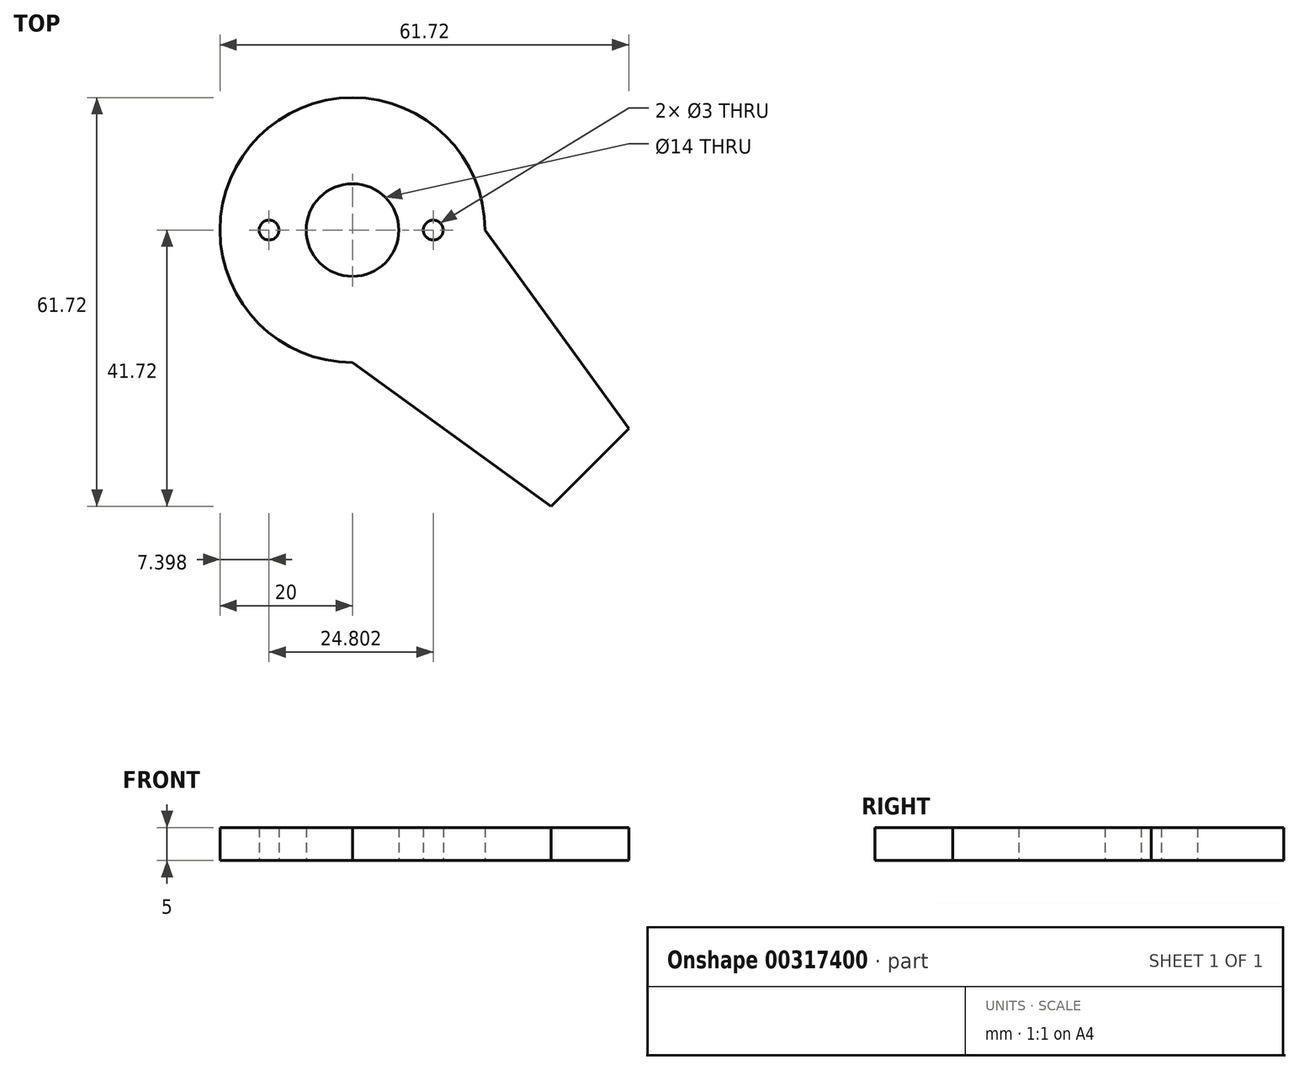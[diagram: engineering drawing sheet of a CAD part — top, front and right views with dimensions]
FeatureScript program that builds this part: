
annotation { "Feature Type Name" : "Feature", "Feature Type Description" : "" }
export const myFeature = defineFeature(function(context is Context, id is Id, definition is map)
    precondition{}
    {
        {
            var Q0;
            Q0=qCreatedBy(makeId("Top.planeOp"),FACE);
            var sketch = newSketch(context, id + "F0", { "sketchPlane" : qUnion([Q0])});
            skLineSegment(sketch, "E0.bottom", {"start": v(0, 0) * mm, "end": v(800, 0) * mm, "construction": true});
            skLineSegment(sketch, "E0.top", {"start": v(0, 800) * mm, "end": v(800, 800) * mm, "construction": true});
            skLineSegment(sketch, "E0.left", {"start": v(0, 0) * mm, "end": v(0, 800) * mm, "construction": true});
            skLineSegment(sketch, "E0.right", {"start": v(800, 0) * mm, "end": v(800, 800) * mm, "construction": true});
            skLineSegment(sketch, "E1.bottom", {"start": v(650, 650) * mm, "end": v(150, 650) * mm, "construction": true});
            skLineSegment(sketch, "E1.top", {"start": v(650, 150) * mm, "end": v(150, 150) * mm, "construction": true});
            skLineSegment(sketch, "E1.left", {"start": v(650, 650) * mm, "end": v(650, 150) * mm, "construction": true});
            skLineSegment(sketch, "E1.right", {"start": v(150, 650) * mm, "end": v(150, 150) * mm, "construction": true});
            skPoint(sketch, "E1.middle", {"position": v(400, 400) * mm});
            skPoint(sketch, "E1.middle.positionSnap0", {"position": v(0, 400) * mm});
            skPoint(sketch, "E1.middle.positionSnap1", {"position": v(400, 800) * mm});
            skPoint(sketch, "E1.centerSnap0", {"position": v(0, 400) * mm});
            skPoint(sketch, "E1.centerSnap1", {"position": v(400, 800) * mm});
            skSolve(sketch);
        }
        {
            var Q0;
            Q0=qCreatedBy(makeId("Top.planeOp"),FACE);
            var sketch = newSketch(context, id + "F1", { "sketchPlane" : qUnion([Q0])});
            skPoint(sketch, "E2", {"position": v(150, 650) * mm});
            skPoint(sketch, "E3", {"position": v(650, 650) * mm});
            skPoint(sketch, "E4", {"position": v(650, 150) * mm});
            skPoint(sketch, "E5", {"position": v(150, 150) * mm});
            skArc(sketch, "E6", {"start": v(250, 650) * mm, "mid": v(79.29, 720.71) * mm, "end": v(150, 550) * mm});
            skArc(sketch, "E7", {"start": v(550, 650) * mm, "mid": v(720.71, 720.71) * mm, "end": v(650, 550) * mm});
            skPoint(sketch, "E8", {"position": v(400, 400) * mm});
            skCircle(sketch, "E9.cCircle", {"center": v(400, 400) * mm, "radius": 100 * mm, "construction": true});
            skLineSegment(sketch, "E9.0", {"start": v(358.58, 500) * mm, "end": v(441.42, 500) * mm});
            skLineSegment(sketch, "E9.1", {"start": v(441.42, 500) * mm, "end": v(500, 441.42) * mm});
            skLineSegment(sketch, "E9.2", {"start": v(500, 441.42) * mm, "end": v(500, 358.58) * mm});
            skLineSegment(sketch, "E9.3", {"start": v(500, 358.58) * mm, "end": v(441.42, 300) * mm});
            skLineSegment(sketch, "E9.4", {"start": v(441.42, 300) * mm, "end": v(358.58, 300) * mm});
            skLineSegment(sketch, "E9.5", {"start": v(358.58, 300) * mm, "end": v(300, 358.58) * mm});
            skLineSegment(sketch, "E9.6", {"start": v(300, 358.58) * mm, "end": v(300, 441.42) * mm});
            skLineSegment(sketch, "E9.7", {"start": v(300, 441.42) * mm, "end": v(358.58, 500) * mm});
            skPoint(sketch, "E9.0.midPoint", {"position": v(400, 500) * mm});
            skLineSegment(sketch, "E10", {"start": v(300, 441.42) * mm, "end": v(150, 550) * mm});
            skLineSegment(sketch, "E11", {"start": v(358.58, 500) * mm, "end": v(250, 650) * mm});
            skLineSegment(sketch, "E12", {"start": v(441.42, 500) * mm, "end": v(550, 650) * mm});
            skLineSegment(sketch, "E13", {"start": v(500, 441.42) * mm, "end": v(650, 550) * mm});
            skLineSegment(sketch, "E14", {"start": v(1227.94, 400) * mm, "end": v(1505.54, 400) * mm, "construction": true});
            skCircle(sketch, "E15", {"center": v(150, 650) * mm, "radius": 35 * mm});
            skCircle(sketch, "E16", {"center": v(650, 650) * mm, "radius": 35 * mm});
            skLineSegment(sketch, "E17.MirrorCS", {"start": v(300, 441.42) * mm, "end": v(300, 358.58) * mm});
            skLineSegment(sketch, "E18.MirrorCS", {"start": v(300, 358.58) * mm, "end": v(358.58, 300) * mm});
            skLineSegment(sketch, "E19.MirrorCS", {"start": v(500, 441.42) * mm, "end": v(441.42, 500) * mm});
            skLineSegment(sketch, "E20.MirrorCS", {"start": v(441.42, 500) * mm, "end": v(358.58, 500) * mm});
            skLineSegment(sketch, "E21.MirrorCS", {"start": v(358.58, 300) * mm, "end": v(441.42, 300) * mm});
            skLineSegment(sketch, "E22.MirrorCS", {"start": v(441.42, 300) * mm, "end": v(500, 358.58) * mm});
            skLineSegment(sketch, "E23.MirrorCS", {"start": v(500, 358.58) * mm, "end": v(500, 441.42) * mm});
            skArc(sketch, "E24.MirrorCS", {"start": v(550, 150) * mm, "mid": v(720.71, 79.29) * mm, "end": v(650, 250) * mm});
            skArc(sketch, "E25.MirrorCS", {"start": v(250, 150) * mm, "mid": v(79.29, 79.29) * mm, "end": v(150, 250) * mm});
            skLineSegment(sketch, "E26.MirrorCS", {"start": v(441.42, 300) * mm, "end": v(550, 150) * mm});
            skLineSegment(sketch, "E27.MirrorCS", {"start": v(500, 358.58) * mm, "end": v(650, 250) * mm});
            skLineSegment(sketch, "E28.MirrorCS", {"start": v(358.58, 500) * mm, "end": v(300, 441.42) * mm});
            skLineSegment(sketch, "E29.MirrorCS", {"start": v(300, 358.58) * mm, "end": v(150, 250) * mm});
            skPoint(sketch, "E30.MirrorP", {"position": v(400, 300) * mm});
            skLineSegment(sketch, "E31.MirrorCS", {"start": v(358.58, 300) * mm, "end": v(250, 150) * mm});
            skCircle(sketch, "E32.MirrorC", {"center": v(650, 150) * mm, "radius": 35 * mm});
            skCircle(sketch, "E33.MirrorC", {"center": v(150, 150) * mm, "radius": 35 * mm});
            skCircle(sketch, "E34", {"center": v(87, 650) * mm, "radius": 7.5 * mm});
            skCircle(sketch, "E35", {"center": v(211, 650) * mm, "radius": 7.5 * mm});
            skCircle(sketch, "E36", {"center": v(590, 650) * mm, "radius": 7.5 * mm});
            skCircle(sketch, "E37", {"center": v(710, 650) * mm, "radius": 7.5 * mm});
            skCircle(sketch, "E38", {"center": v(76.51, 150) * mm, "radius": 7.5 * mm});
            skCircle(sketch, "E39", {"center": v(219.98, 150) * mm, "radius": 7.5 * mm});
            skCircle(sketch, "E40", {"center": v(579.97, 150) * mm, "radius": 12.44 * mm});
            skCircle(sketch, "E41", {"center": v(710.5, 150) * mm, "radius": 11.04 * mm});
            skSolve(sketch);
        }
        {
            var Q0;
            Q0=makeQuery(id+"F1.imprint","IMPRINT",FACE,{"disambiguationData":[TD([[makeQuery(id+"F1.imprint","IMPRINT",EDGE,{"derivedFrom":sQuery(id+"F1.wireOp",EDGE,"E6")}),1.0]])]});
            var Q1;
            Q1=makeQuery(id+"F1.imprint","IMPRINT",FACE,{"disambiguationData":[TD([[makeQuery(id+"F1.imprint","IMPRINT",EDGE,{"derivedFrom":sQuery(id+"F1.wireOp",EDGE,"E17.MirrorCS")}),1.0]])]});
            var Q2;
            Q2=makeQuery(id+"F1.imprint","IMPRINT",FACE,{"disambiguationData":[TD([[makeQuery(id+"F1.imprint","IMPRINT",EDGE,{"derivedFrom":sQuery(id+"F1.wireOp",EDGE,"E7")}),-1.0]])]});
            var Q3;
            Q3=makeQuery(id+"F1.imprint","IMPRINT",FACE,{"disambiguationData":[TD([[makeQuery(id+"F1.imprint","IMPRINT",EDGE,{"derivedFrom":sQuery(id+"F1.wireOp",EDGE,"E18.MirrorCS")}),-1.0]])]});
            var Q4;
            Q4=makeQuery(id+"F1.imprint","IMPRINT",FACE,{"disambiguationData":[TD([[makeQuery(id+"F1.imprint","IMPRINT",EDGE,{"derivedFrom":sQuery(id+"F1.wireOp",EDGE,"E22.MirrorCS")}),-1.0]])]});
            extrude(context, id + "F2", {"entities" : qUnion([Q0, Q1, Q2, Q3, Q4]), "depth" : 25 * mm});
        }
        {
            var Q0;
            Q0=makeQuery(id+"F2.opExtrude","SWEPT_BODY",BODY,{"disambiguationData":[OSD([sQuery(id+"F1.wireOp",EDGE,"E6"),sQuery(id+"F1.wireOp",EDGE,"E7"),sQuery(id+"F1.wireOp",EDGE,"E10"),sQuery(id+"F1.wireOp",EDGE,"E11"),sQuery(id+"F1.wireOp",EDGE,"E12"),sQuery(id+"F1.wireOp",EDGE,"E13"),sQuery(id+"F1.wireOp",EDGE,"E15"),sQuery(id+"F1.wireOp",EDGE,"E16"),sQuery(id+"F1.wireOp",EDGE,"E17.MirrorCS"),sQuery(id+"F1.wireOp",EDGE,"E20.MirrorCS"),sQuery(id+"F1.wireOp",EDGE,"E21.MirrorCS"),sQuery(id+"F1.wireOp",EDGE,"E23.MirrorCS"),sQuery(id+"F1.wireOp",EDGE,"E24.MirrorCS"),sQuery(id+"F1.wireOp",EDGE,"E25.MirrorCS"),sQuery(id+"F1.wireOp",EDGE,"E26.MirrorCS"),sQuery(id+"F1.wireOp",EDGE,"E27.MirrorCS"),sQuery(id+"F1.wireOp",EDGE,"E29.MirrorCS"),sQuery(id+"F1.wireOp",EDGE,"E31.MirrorCS"),sQuery(id+"F1.wireOp",EDGE,"E32.MirrorC"),sQuery(id+"F1.wireOp",EDGE,"E33.MirrorC"),sQuery(id+"F1.wireOp",EDGE,"E34"),sQuery(id+"F1.wireOp",EDGE,"E35"),sQuery(id+"F1.wireOp",EDGE,"E36"),sQuery(id+"F1.wireOp",EDGE,"E37"),sQuery(id+"F1.wireOp",EDGE,"E38"),sQuery(id+"F1.wireOp",EDGE,"E39"),sQuery(id+"F1.wireOp",EDGE,"E40"),sQuery(id+"F1.wireOp",EDGE,"E41")])]});
            var Q1;
            Q1=qCreatedBy(makeId("Origin.pointOp"),VERTEX);
            transform(context, id + "F3", {"entities" : qUnion([Q0]), "transformType" : TransformType.SCALE_UNIFORMLY, "scale" : 0.2, "scalePoint" : qUnion([Q1]), "makeCopy" : false});
        }
    });
